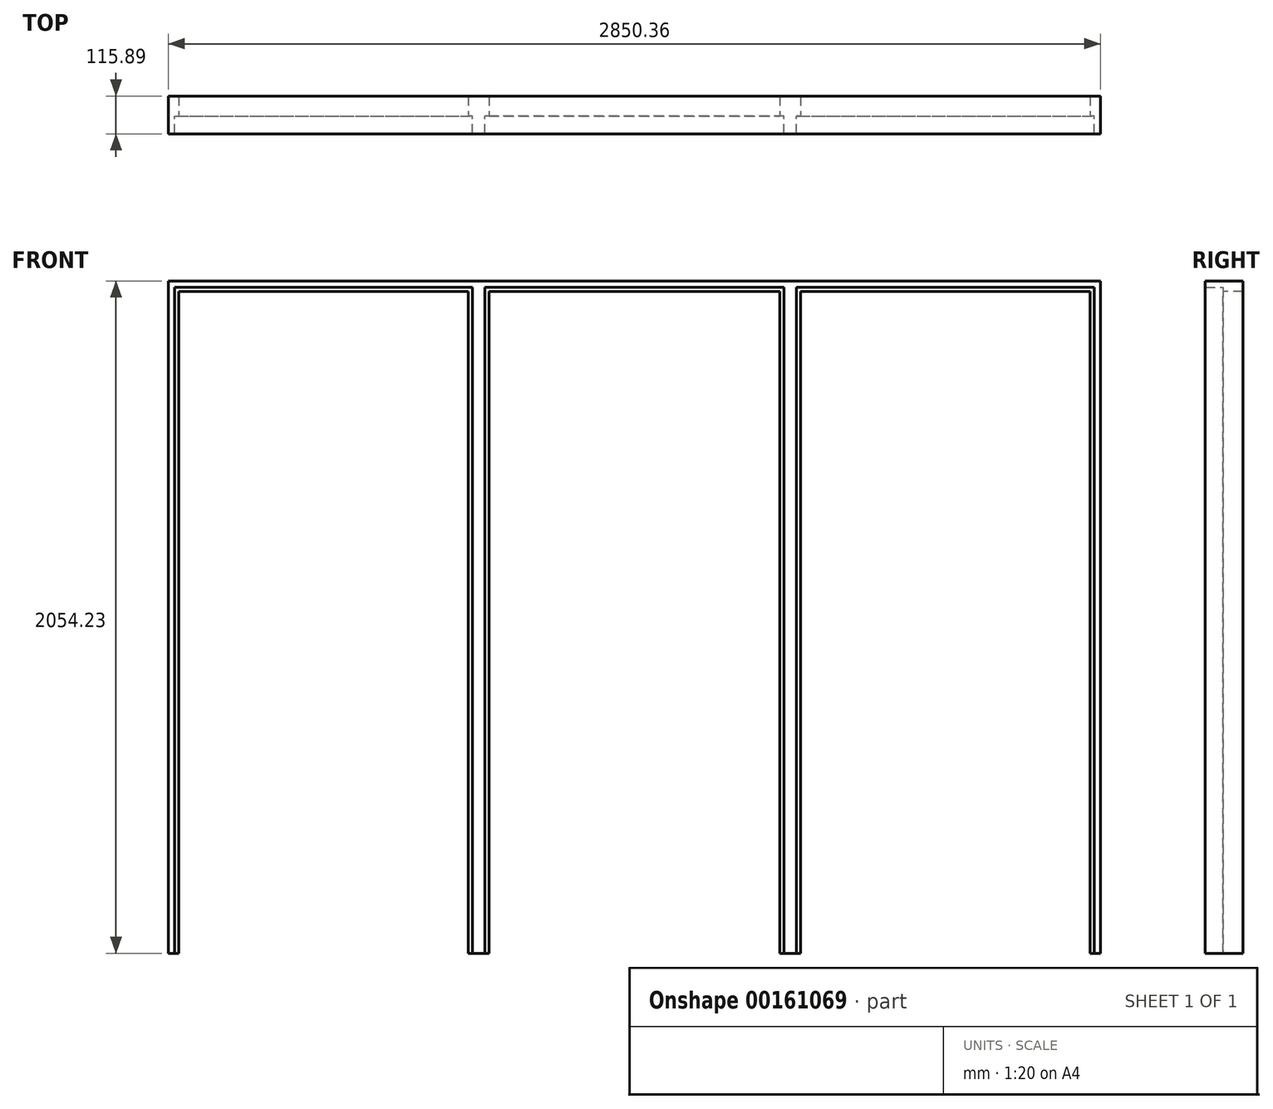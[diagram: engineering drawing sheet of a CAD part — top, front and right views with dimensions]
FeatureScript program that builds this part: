
annotation { "Feature Type Name" : "Feature", "Feature Type Description" : "" }
export const myFeature = defineFeature(function(context is Context, id is Id, definition is map)
    precondition{}
    {
        {
            var Q0;
            Q0=qCreatedBy(makeId("Front.planeOp"),FACE);
            cPlane(context, id + "F0", {"entities" : qUnion([Q0]), "cplaneType" : CPlaneType.OFFSET, "offset" : 3.17 * mm, "oppositeDirection" : true, "width" : 152.4 * mm, "height" : 152.4 * mm});
        }
        {
            var Q0;
            Q0=qCreatedBy(makeId("Front.planeOp"),FACE);
            var sketch = newSketch(context, id + "F1", { "sketchPlane" : qUnion([Q0])});
            skLineSegment(sketch, "E0.bottom", {"start": v(0, 0) * mm, "end": v(19.05, 0) * mm});
            skLineSegment(sketch, "E0.top", {"start": v(0, 2035.18) * mm, "end": v(19.05, 2035.18) * mm});
            skLineSegment(sketch, "E0.left", {"start": v(0, 0) * mm, "end": v(0, 2035.18) * mm});
            skLineSegment(sketch, "E0.right", {"start": v(19.05, 0) * mm, "end": v(19.05, 2035.18) * mm});
            skLineSegment(sketch, "E1.bottom", {"start": v(31.75, 2022.48) * mm, "end": v(19.05, 2022.48) * mm});
            skLineSegment(sketch, "E1.top", {"start": v(31.75, 0) * mm, "end": v(19.05, 0) * mm});
            skLineSegment(sketch, "E1.left", {"start": v(31.75, 2022.48) * mm, "end": v(31.75, 0) * mm});
            skLineSegment(sketch, "E1.right", {"start": v(19.05, 2022.48) * mm, "end": v(19.05, 0) * mm});
            skLineSegment(sketch, "E2.bottom", {"start": v(0, 2035.18) * mm, "end": v(2850.36, 2035.18) * mm});
            skLineSegment(sketch, "E2.top", {"start": v(0, 2054.23) * mm, "end": v(2850.36, 2054.23) * mm});
            skLineSegment(sketch, "E2.left", {"start": v(0, 2035.18) * mm, "end": v(0, 2054.23) * mm});
            skLineSegment(sketch, "E2.right", {"start": v(2850.36, 2035.18) * mm, "end": v(2850.36, 2054.23) * mm});
            skPoint(sketch, "E3.oppositeSnap0", {"position": v(9.53, 0) * mm});
            skLineSegment(sketch, "E3.bottom", {"start": v(2850.36, 2035.18) * mm, "end": v(2831.3, 2035.18) * mm});
            skLineSegment(sketch, "E3.top", {"start": v(2850.36, 0) * mm, "end": v(2831.3, 0) * mm});
            skLineSegment(sketch, "E3.left", {"start": v(2850.36, 2035.18) * mm, "end": v(2850.36, 0) * mm});
            skLineSegment(sketch, "E3.right", {"start": v(2831.3, 2035.18) * mm, "end": v(2831.3, 0) * mm});
            skLineSegment(sketch, "E4.bottom", {"start": v(2831.3, 0) * mm, "end": v(2818.6, 0) * mm});
            skLineSegment(sketch, "E4.top", {"start": v(2831.3, 2022.48) * mm, "end": v(2818.6, 2022.48) * mm});
            skLineSegment(sketch, "E4.left", {"start": v(2831.3, 0) * mm, "end": v(2831.3, 2022.48) * mm});
            skLineSegment(sketch, "E4.right", {"start": v(2818.6, 0) * mm, "end": v(2818.6, 2022.48) * mm});
            skLineSegment(sketch, "E5.bottom", {"start": v(19.05, 2035.18) * mm, "end": v(2831.3, 2035.18) * mm});
            skLineSegment(sketch, "E5.left", {"start": v(19.05, 2035.18) * mm, "end": v(19.05, 2022.48) * mm});
            skLineSegment(sketch, "E5.right", {"start": v(2831.3, 2035.18) * mm, "end": v(2831.3, 2022.48) * mm});
            skLineSegment(sketch, "E6.bottom", {"start": v(949.32, 2035.18) * mm, "end": v(930.27, 2035.18) * mm});
            skLineSegment(sketch, "E6.top", {"start": v(949.32, 0) * mm, "end": v(930.27, 0) * mm});
            skLineSegment(sketch, "E6.left", {"start": v(949.32, 2035.18) * mm, "end": v(949.32, 0) * mm});
            skLineSegment(sketch, "E6.right", {"start": v(930.27, 2035.18) * mm, "end": v(930.28, 0) * mm});
            skLineSegment(sketch, "E7.bottom", {"start": v(930.27, 0) * mm, "end": v(917.57, 0) * mm});
            skLineSegment(sketch, "E7.top", {"start": v(930.27, 2022.48) * mm, "end": v(917.57, 2022.48) * mm});
            skLineSegment(sketch, "E7.left", {"start": v(930.27, 0) * mm, "end": v(930.27, 2022.48) * mm});
            skLineSegment(sketch, "E7.right", {"start": v(917.57, 0) * mm, "end": v(917.57, 2022.48) * mm});
            skLineSegment(sketch, "E8.bottom", {"start": v(949.32, 2035.18) * mm, "end": v(968.38, 2035.18) * mm});
            skLineSegment(sketch, "E8.top", {"start": v(949.32, 0) * mm, "end": v(968.38, 0) * mm});
            skLineSegment(sketch, "E8.right", {"start": v(968.37, 2035.18) * mm, "end": v(968.38, 0) * mm});
            skLineSegment(sketch, "E9.bottom", {"start": v(968.38, 0) * mm, "end": v(981.08, 0) * mm});
            skLineSegment(sketch, "E9.top", {"start": v(968.37, 2022.48) * mm, "end": v(981.07, 2022.48) * mm});
            skLineSegment(sketch, "E9.left", {"start": v(968.38, 0) * mm, "end": v(968.37, 2022.48) * mm});
            skLineSegment(sketch, "E9.right", {"start": v(981.08, 0) * mm, "end": v(981.07, 2022.48) * mm});
            skLineSegment(sketch, "E10.bottom", {"start": v(1901.03, 2035.18) * mm, "end": v(1881.98, 2035.18) * mm});
            skLineSegment(sketch, "E10.top", {"start": v(1901.03, 0) * mm, "end": v(1881.98, 0) * mm});
            skLineSegment(sketch, "E10.left", {"start": v(1901.03, 2035.18) * mm, "end": v(1901.03, 0) * mm});
            skLineSegment(sketch, "E10.right", {"start": v(1881.98, 2035.18) * mm, "end": v(1881.98, 0) * mm});
            skLineSegment(sketch, "E11.bottom", {"start": v(1901.03, 0) * mm, "end": v(1920.08, 0) * mm});
            skLineSegment(sketch, "E11.top", {"start": v(1901.03, 2035.18) * mm, "end": v(1920.08, 2035.18) * mm});
            skLineSegment(sketch, "E11.left", {"start": v(1901.03, 0) * mm, "end": v(1901.03, 2035.18) * mm});
            skLineSegment(sketch, "E11.right", {"start": v(1920.08, 0) * mm, "end": v(1920.08, 2035.18) * mm});
            skLineSegment(sketch, "E12.bottom", {"start": v(1881.98, 2022.48) * mm, "end": v(1869.28, 2022.48) * mm});
            skLineSegment(sketch, "E12.top", {"start": v(1881.98, 0) * mm, "end": v(1869.28, 0) * mm});
            skLineSegment(sketch, "E12.left", {"start": v(1881.98, 2022.48) * mm, "end": v(1881.98, 0) * mm});
            skLineSegment(sketch, "E12.right", {"start": v(1869.28, 2022.48) * mm, "end": v(1869.28, 0) * mm});
            skLineSegment(sketch, "E13.bottom", {"start": v(1920.08, 0) * mm, "end": v(1932.78, 0) * mm});
            skLineSegment(sketch, "E13.top", {"start": v(1920.08, 2022.48) * mm, "end": v(1932.78, 2022.48) * mm});
            skLineSegment(sketch, "E13.left", {"start": v(1920.08, 0) * mm, "end": v(1920.08, 2022.48) * mm});
            skLineSegment(sketch, "E13.right", {"start": v(1932.78, 0) * mm, "end": v(1932.78, 2022.48) * mm});
            skLineSegment(sketch, "E14.bottom", {"start": v(19.05, 2035.18) * mm, "end": v(930.27, 2035.18) * mm});
            skLineSegment(sketch, "E14.top", {"start": v(19.05, 2022.48) * mm, "end": v(930.27, 2022.48) * mm});
            skLineSegment(sketch, "E14.right", {"start": v(930.27, 2035.18) * mm, "end": v(930.27, 2022.48) * mm});
            skLineSegment(sketch, "E15.bottom", {"start": v(968.38, 2035.18) * mm, "end": v(1881.98, 2035.18) * mm});
            skLineSegment(sketch, "E15.top", {"start": v(968.37, 2022.48) * mm, "end": v(1881.98, 2022.48) * mm});
            skLineSegment(sketch, "E15.left", {"start": v(968.37, 2035.18) * mm, "end": v(968.37, 2022.48) * mm});
            skLineSegment(sketch, "E15.right", {"start": v(1881.98, 2035.18) * mm, "end": v(1881.98, 2022.48) * mm});
            skLineSegment(sketch, "E16.bottom", {"start": v(1920.08, 2035.18) * mm, "end": v(2831.3, 2035.18) * mm});
            skLineSegment(sketch, "E16.top", {"start": v(1920.08, 2022.48) * mm, "end": v(2831.3, 2022.48) * mm});
            skLineSegment(sketch, "E16.left", {"start": v(1920.08, 2035.18) * mm, "end": v(1920.08, 2022.48) * mm});
            skSolve(sketch);
        }
        {
            var Q0;
            Q0=qCreatedBy(id+"F0.planeOp",FACE);
            var sketch = newSketch(context, id + "F2", { "sketchPlane" : qUnion([Q0])});
            skLineSegment(sketch, "E17.0", {"start": v(0, 0) * mm, "end": v(0, 2035.18) * mm});
            skLineSegment(sketch, "E18.0", {"start": v(0, 0) * mm, "end": v(19.05, 0) * mm});
            skLineSegment(sketch, "E19.0", {"start": v(31.75, 0) * mm, "end": v(19.05, 0) * mm});
            skLineSegment(sketch, "E20.0", {"start": v(31.75, 2022.47) * mm, "end": v(31.75, 0) * mm});
            skLineSegment(sketch, "E21.0", {"start": v(19.05, 2022.48) * mm, "end": v(930.27, 2022.48) * mm});
            skLineSegment(sketch, "E22.0", {"start": v(917.57, 0) * mm, "end": v(917.57, 2022.48) * mm});
            skLineSegment(sketch, "E23.0", {"start": v(0, 2054.23) * mm, "end": v(2850.36, 2054.23) * mm});
            skLineSegment(sketch, "E24.0", {"start": v(0, 2035.18) * mm, "end": v(0, 2054.23) * mm});
            skLineSegment(sketch, "E25.0", {"start": v(968.37, 2022.48) * mm, "end": v(1881.98, 2022.48) * mm});
            skLineSegment(sketch, "E26.0", {"start": v(981.08, 0) * mm, "end": v(981.07, 2022.48) * mm});
            skLineSegment(sketch, "E27.0", {"start": v(1869.28, 2022.48) * mm, "end": v(1869.28, 0) * mm});
            skLineSegment(sketch, "E28.0", {"start": v(1932.78, 0) * mm, "end": v(1932.78, 2022.48) * mm});
            skLineSegment(sketch, "E29.0", {"start": v(1920.08, 2022.48) * mm, "end": v(2831.3, 2022.48) * mm});
            skLineSegment(sketch, "E30.0", {"start": v(2818.6, 0) * mm, "end": v(2818.6, 2022.48) * mm});
            skLineSegment(sketch, "E31.0", {"start": v(2850.36, 2035.18) * mm, "end": v(2850.36, 0) * mm});
            skLineSegment(sketch, "E32.0", {"start": v(2850.36, 2035.18) * mm, "end": v(2850.36, 2054.23) * mm});
            skLineSegment(sketch, "E33.0", {"start": v(930.27, 0) * mm, "end": v(917.57, 0) * mm});
            skLineSegment(sketch, "E34.0", {"start": v(949.32, 0) * mm, "end": v(930.27, 0) * mm});
            skLineSegment(sketch, "E35.0", {"start": v(949.32, 0) * mm, "end": v(968.38, 0) * mm});
            skLineSegment(sketch, "E36.0", {"start": v(968.38, 0) * mm, "end": v(981.08, 0) * mm});
            skLineSegment(sketch, "E37.0", {"start": v(1881.98, 0) * mm, "end": v(1869.28, 0) * mm});
            skLineSegment(sketch, "E38.0", {"start": v(1901.03, 0) * mm, "end": v(1881.98, 0) * mm});
            skLineSegment(sketch, "E39.0", {"start": v(1901.03, 0) * mm, "end": v(1920.08, 0) * mm});
            skLineSegment(sketch, "E40.0", {"start": v(1920.08, 0) * mm, "end": v(1932.78, 0) * mm});
            skLineSegment(sketch, "E41.0", {"start": v(2831.3, 0) * mm, "end": v(2818.6, 0) * mm});
            skLineSegment(sketch, "E42.0", {"start": v(2850.36, 0) * mm, "end": v(2831.3, 0) * mm});
            skSolve(sketch);
        }
        {
            var Q0;
            Q0=qSketchRegion(id+"F2",true);
            extrude(context, id + "F3", {"entities" : qUnion([Q0]), "oppositeDirection" : true, "depth" : 61.9 * mm});
        }
        {
            var Q0;
            Q0=qCreatedBy(makeId("Front.planeOp"),FACE);
            var sketch = newSketch(context, id + "F4", { "sketchPlane" : qUnion([Q0])});
            skLineSegment(sketch, "E43.0", {"start": v(0, 0) * mm, "end": v(19.05, 0) * mm});
            skLineSegment(sketch, "E44.0", {"start": v(19.05, 2022.48) * mm, "end": v(19.05, 0) * mm});
            skLineSegment(sketch, "E45.0", {"start": v(0, 0) * mm, "end": v(0, 2035.18) * mm});
            skLineSegment(sketch, "E46.0", {"start": v(0, 2035.18) * mm, "end": v(0, 2054.23) * mm});
            skLineSegment(sketch, "E47.0", {"start": v(0, 2054.23) * mm, "end": v(2850.36, 2054.23) * mm});
            skLineSegment(sketch, "E48.0", {"start": v(19.05, 2035.18) * mm, "end": v(19.05, 2022.48) * mm});
            skLineSegment(sketch, "E49.0", {"start": v(19.05, 2035.18) * mm, "end": v(930.27, 2035.18) * mm});
            skLineSegment(sketch, "E50.0", {"start": v(930.27, 2035.18) * mm, "end": v(930.28, 0) * mm});
            skLineSegment(sketch, "E51.0", {"start": v(968.37, 2035.18) * mm, "end": v(968.38, 0) * mm});
            skLineSegment(sketch, "E52.0", {"start": v(949.32, 0) * mm, "end": v(930.27, 0) * mm});
            skLineSegment(sketch, "E53.0", {"start": v(949.32, 0) * mm, "end": v(968.38, 0) * mm});
            skLineSegment(sketch, "E54.0", {"start": v(1881.98, 2035.18) * mm, "end": v(1881.98, 2022.48) * mm});
            skLineSegment(sketch, "E55.0", {"start": v(1881.98, 2022.48) * mm, "end": v(1881.98, 0) * mm});
            skLineSegment(sketch, "E56.0", {"start": v(1920.08, 2035.18) * mm, "end": v(1920.08, 2022.48) * mm});
            skLineSegment(sketch, "E57.0", {"start": v(1920.08, 0) * mm, "end": v(1920.08, 2022.48) * mm});
            skLineSegment(sketch, "E58.0", {"start": v(2831.3, 2035.18) * mm, "end": v(2831.3, 2022.48) * mm});
            skLineSegment(sketch, "E59.0", {"start": v(2831.3, 0) * mm, "end": v(2831.3, 2022.48) * mm});
            skLineSegment(sketch, "E60.0", {"start": v(2850.36, 2035.18) * mm, "end": v(2850.36, 0) * mm});
            skPoint(sketch, "E61.0", {"position": v(2850.36, 2044.7) * mm});
            skLineSegment(sketch, "E62.0", {"start": v(2850.36, 2035.18) * mm, "end": v(2850.36, 2054.23) * mm});
            skLineSegment(sketch, "E63", {"start": v(1920.08, 2035.18) * mm, "end": v(2831.3, 2035.18) * mm});
            skLineSegment(sketch, "E64", {"start": v(1881.98, 2035.18) * mm, "end": v(968.37, 2035.18) * mm});
            skLineSegment(sketch, "E65.0", {"start": v(1901.03, 0) * mm, "end": v(1881.98, 0) * mm});
            skLineSegment(sketch, "E66.0", {"start": v(1901.03, 0) * mm, "end": v(1920.08, 0) * mm});
            skLineSegment(sketch, "E67.0", {"start": v(2850.36, 0) * mm, "end": v(2831.3, 0) * mm});
            skSolve(sketch);
        }
        {
            var Q0;
            Q0=qSketchRegion(id+"F4",true);
            extrude(context, id + "F5", {"entities" : qUnion([Q0]), "operationType" : NewBodyOperationType.ADD, "depth" : 50.8 * mm, "hasSecondDirection" : true, "secondDirectionOppositeDirection" : true, "secondDirectionDepth" : 3.17 * mm});
        }
    });
